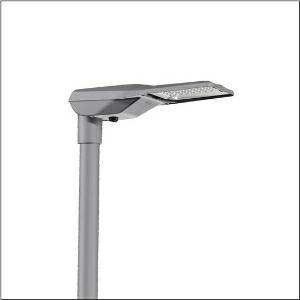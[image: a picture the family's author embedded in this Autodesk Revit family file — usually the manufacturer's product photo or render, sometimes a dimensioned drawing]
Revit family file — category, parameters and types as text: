
# Revit family: streetlight_sl_21_iq_mini___st1_0a_5xe2d31u08hb_e98e
name_source: partatom
category: Lighting Fixtures
units: mm (PartAtom-declared; Revit-internal decimal feet)

## family parameters
Cut with Voids When Loaded = No
Host = Face
Light Source = No
Part Type = Normal
Room Calculation Point = No
Round Connector Dimension = Use Diameter
Shared = No

## types (1)
- --- (1 x LED, 9750 lm, 71 W, 3000K)
    Apparent Load = 71 VA
    CIE Flux Codes = 37 72 97 100 100
    Color Rendering = 70
    Color Temperature = 3000K
    Default Elevation = 1800 mm
    Description = Streetlight SL 21 iQ mini, mast luminaire, primary light control with lens, of PMMA, primary optical cover: cover, of toughened safety glass, transparent, light distribution: ST1.0a, light emission: direct distribution, primary light characteristic: asymmetric, installation type: post-top, side-entry, LED, High Power LED, rated luminous flux: 9.750lm, luminous efficacy: 137lm/W, light colour: 730, colour temperature: 3000K, control gear: iQ-Street Remote, D4i with power reduction, control: pre-setting: logarithmic dimming characteristic, Street-Remote, Auto-Match, Temp-Guard, Lumen-Switch, Night-Set, Smart-Wire, Light-Fading, Desk-Remote (wireless, voltage-free reading and setting of iQ features in the workshop via application-optimized NFC function/RFID function), optimised constant luminous flux control (CLO 2.0), mains connection: 220..240V, AC, 50/60Hz, start of lifetime: 71W, end of service life: 75W, reduction: 30W, luminaire housing, of diecast aluminium, powder-coated, Siteco® metallic grey (DB 702S), corrosivity category C5 mid according to DIN EN ISO 12944, please order mast flange separately, inclination adjustable: 0°, 5°, 10°, 15°, sealing non-destructively replaceable, multi-level sealing system, length: 628mm, width: 235mm, height: 110mm, mast flange for spigot size: 42mm (side-entry): 5XC10008XM4, 60/48mm (side-entry/post-top): 5XC10108XM2, 76/60mm (side-entry/post-top): 5XC10108XM1, mounting height: 4..8m, Smart Interface below, protection rating (complete): IP66, insulation class (complete): insulation class II (safety insulation), certification: CE, ENEC, ENEC+, VDE, impact resistance: IK10, permissible operating ambient temperature for outdoor applications: -40..+50°C, standard-compliant lighting for roads and squares, packaging unit: 1 piece

Light Distribution: ST1.0a
    Height = 110 mm
    Lamp = 1 x LED
    Lamp Light Flux = 9750 lm
    Lamp Power = 71 W
    Lamp count = 1
    Length = 625 mm
    Luminous efficacy = 137 lm/W
    Manufacturer = Siteco
    ModVariant = No
    Model = 5XE2D31U08HB
    Number of Poles = 1
    OnlyDefault = Yes
    Power Factor = 1
    Product Name = Streetlight SL 21 iQ mini | ST1.0a
    Product group = mast luminaire | pylon top
    ProductGroupID = 6100
    Protection Class = Protection class II
    Protection Degree = IP 66
    RLX_Detail_Level = 1
    RLX_Emergency_Light_Flux = 0 lm
    RLX_Emergency_Type = 0
    RLX_Emergency_Type_DB = No
    RlxData = <blob elided: 93217 chars, md5=ae92d277>
    Socket = socket
    Standby Power = 0 W
    System Light Flux = 9750 lm
    System Power = 71 W
    Type Comments = factory setting: luminous flux: 100 % | dim-lin: 254 | 716 mA
    Type Image = l_1003516.jpg
    URL = http://relux.com
    VarID = @adj_136665
    Voltage = 0 V
    Weight = 0.00 kg
    Width = 234 mm

## geometry (parser evidence)
native form markers: Blend x4, Sweep x11
no freeform markers — native parametric forms only
